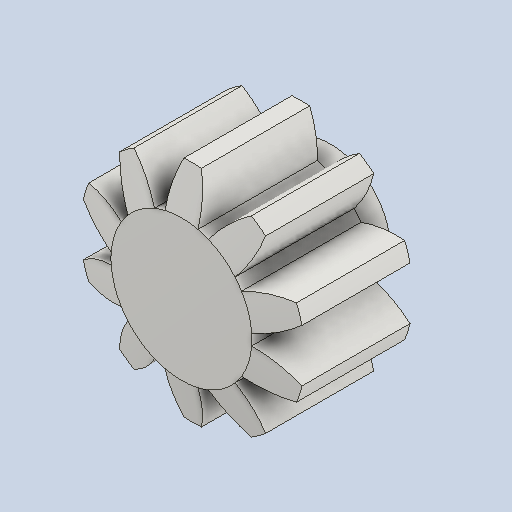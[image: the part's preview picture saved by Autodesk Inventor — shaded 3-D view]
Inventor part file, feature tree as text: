
AUTODESK INVENTOR PART (.ipt)
format: ipt  version: 2022 (Build 260153000, 153)  size: 569,344 bytes
history: native  units: mm (DEFAULTED — no unit token found)
features: sketch x6, extrude x4, plane x3, other x3, projected_geometry x2, revolve x1
ambient origin geometry x8: Origin, YZ Plane, XZ Plane, XY Plane, X Axis, Y Axis, Z Axis, Center Point
bodies: Solid1 (feature_tree)
feature tree (19):
  extrude  "Extrusion1"  Depth=6.35mm TaperAngle=0.0deg
  plane  "Work Plane1"
  plane  "Work Plane2"
  plane  "Work Plane3"
  other  "Spur Gear"
  extrude  "Extrusion2"  Depth=10.0mm TaperAngle=0.0deg
  extrude  "Extrusion3"  TaperAngle=0.0deg  [1 undecoded]
  revolve  "Revolution1"  [1 undecoded]
  extrude  "Extrusion4"  TaperAngle=0.0deg  [1 undecoded]
  sketch  "Sketch1"  dims[d0=11.961303mm d1=6.35mm d2=0.0mm]
  sketch  "Sketch2"  dims[d3=10.0mm d4=76.2mm d5=0.0mm]
  other  "Srf1"
  sketch  "Sketch3"  dims[d6=0.0mm d7=3.141593mm d9=0.0mm]
  sketch  "Sketch4"  dims[d14=0.0mm d15=23.75408mm]
  projected_geometry  "Projected Loop1"
  sketch  "Sketch5"  dims[d16=0.0mm d17=0.0mm]
  sketch  "Sketch6"  dims[d18=0.0mm d19=23.75408mm d20=3.325mm d21=0.0mm d22=0.0mm d23=6.35mm d24=1.5875mm d25=0.0mm d26=15.0deg d27=90.0deg d28=2.0mm d29=0.0mm]
  projected_geometry  "Projected Loop2"
  other  "Pitch Diameter"
note: 3 required parameter values undecoded (feature->parameter linkage not recoverable at this tier; creation-order binding heuristic only, values carry confidence <= 0.55)